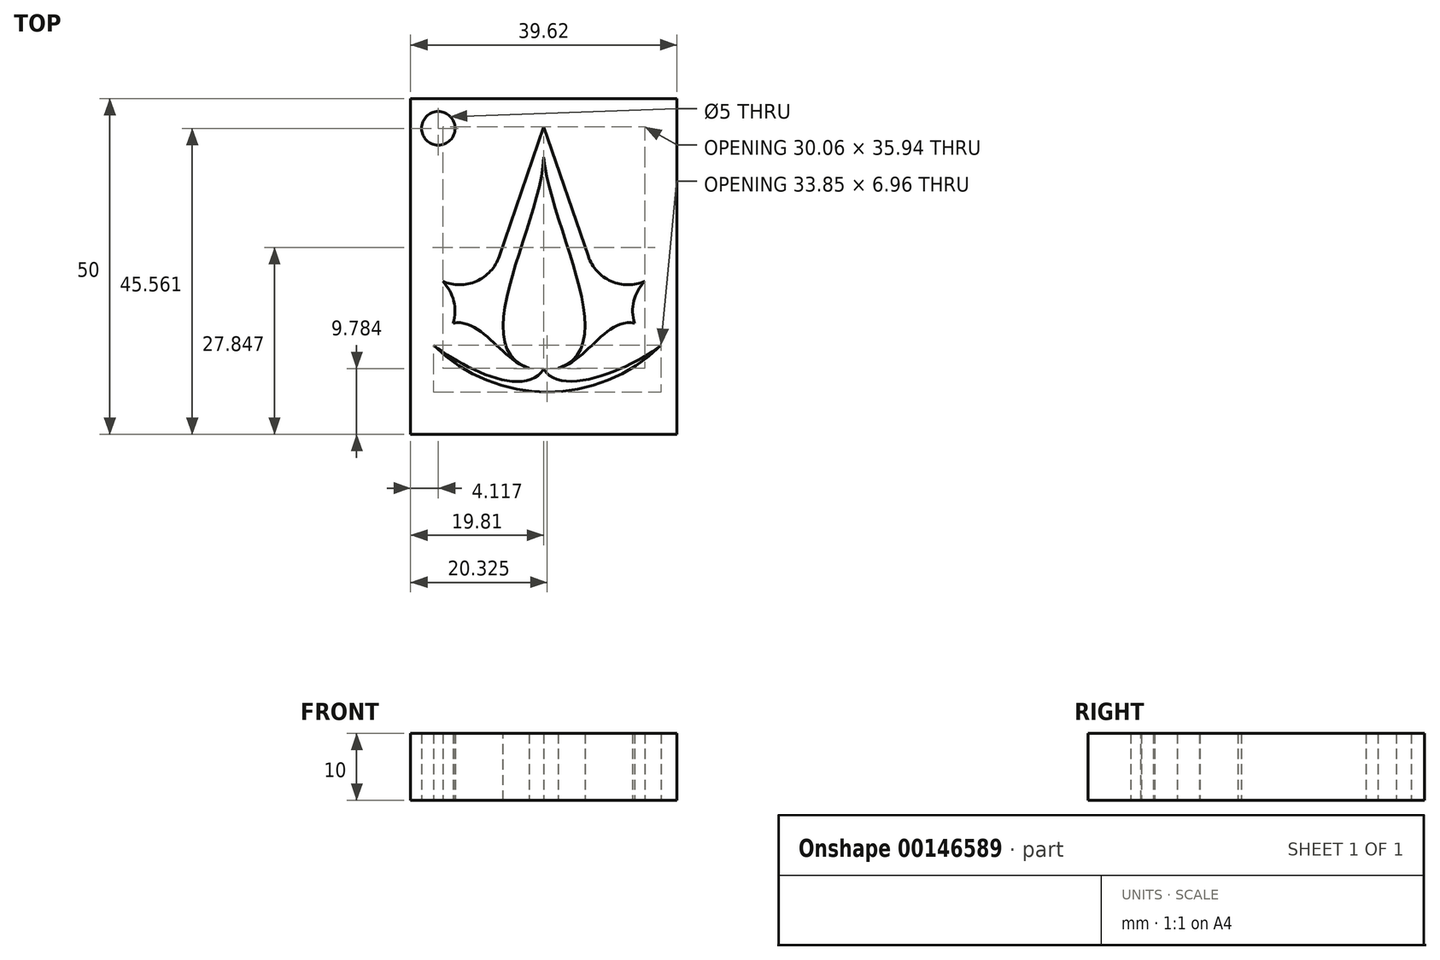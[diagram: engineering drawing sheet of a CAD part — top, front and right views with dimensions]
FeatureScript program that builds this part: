
annotation { "Feature Type Name" : "Feature", "Feature Type Description" : "" }
export const myFeature = defineFeature(function(context is Context, id is Id, definition is map)
    precondition{}
    {
        {
            var Q0;
            Q0=qCreatedBy(makeId("Top.planeOp"),FACE);
            var sketch = newSketch(context, id + "F0", { "sketchPlane" : qUnion([Q0])});
            skPoint(sketch, "E0", {"position": v(0, 23.04) * mm});
            skLineSegment(sketch, "E1", {"start": v(0, 23.04) * mm, "end": v(-6.63, 3.72) * mm});
            skLineSegment(sketch, "E2", {"start": v(0, 23.04) * mm, "end": v(6.63, 3.72) * mm});
            skPoint(sketch, "E3", {"position": v(-15.03, 0) * mm});
            skPoint(sketch, "E4", {"position": v(15.03, 0) * mm});
            skArc(sketch, "E5", {"start": v(-15.03, 0) * mm, "mid": v(-10.02, 0.03) * mm, "end": v(-6.63, 3.72) * mm});
            skArc(sketch, "E6", {"start": v(6.63, 3.72) * mm, "mid": v(10.02, 0.03) * mm, "end": v(15.03, 0) * mm});
            skPoint(sketch, "E7", {"position": v(-13.48, -6.24) * mm});
            skPoint(sketch, "E8", {"position": v(13.48, -6.24) * mm});
            skArc(sketch, "E9", {"start": v(-13.48, -6.24) * mm, "mid": v(-13.4, -2.9) * mm, "end": v(-15.03, 0) * mm});
            skArc(sketch, "E10", {"start": v(15.03, 0) * mm, "mid": v(13.4, -2.9) * mm, "end": v(13.48, -6.24) * mm});
            skPoint(sketch, "E11", {"position": v(0, -6.24) * mm});
            skLineSegment(sketch, "E12", {"start": v(0, -6.24) * mm, "end": v(-13.48, -6.24) * mm, "construction": true});
            skLineSegment(sketch, "E13", {"start": v(0, -6.24) * mm, "end": v(13.48, -6.24) * mm, "construction": true});
            skPoint(sketch, "E14", {"position": v(0, 3.72) * mm});
            skLineSegment(sketch, "E15", {"start": v(-6.63, 3.72) * mm, "end": v(0, 3.72) * mm, "construction": true});
            skLineSegment(sketch, "E16", {"start": v(0, 3.72) * mm, "end": v(6.63, 3.72) * mm, "construction": true});
            skPoint(sketch, "E17", {"position": v(-2.15, -12.9) * mm});
            skPoint(sketch, "E18", {"position": v(2.15, -12.9) * mm});
            skFitSpline(sketch, "E19", {"points": [v(-13.48, -6.24) * mm, v(-2.15, -12.9) * mm], "startDerivative": vector(12.7, 2.7) * mm, "endDerivative": vector(11.86, -2.84) * mm});
            skFitSpline(sketch, "E20", {"points": [v(13.48, -6.24) * mm, v(2.15, -12.9) * mm], "startDerivative": vector(-12.78, 2.7) * mm, "endDerivative": vector(-12.82, -2.84) * mm});
            skPoint(sketch, "E21", {"position": v(0, 18.52) * mm});
            skFitSpline(sketch, "E22", {"points": [v(-2.15, -12.9) * mm, v(0, 18.52) * mm], "startDerivative": vector(-29.03, 9.1) * mm, "endDerivative": vector(1.52, 31.2) * mm});
            skFitSpline(sketch, "E23", {"points": [v(2.15, -12.9) * mm, v(0, 18.52) * mm], "startDerivative": vector(28.93, 9.1) * mm, "endDerivative": vector(-2.78, 31.2) * mm});
            skPoint(sketch, "E24", {"position": v(0, -13.07) * mm});
            skPoint(sketch, "E25", {"position": v(-16.4, -9.52) * mm});
            skPoint(sketch, "E26", {"position": v(17.44, -9.52) * mm});
            skArc(sketch, "E27", {"start": v(-16.4, -9.52) * mm, "mid": v(0.52, -16.48) * mm, "end": v(17.44, -9.52) * mm});
            skFitSpline(sketch, "E28", {"points": [v(0, -13.07) * mm, v(-16.4, -9.52) * mm], "startDerivative": vector(-8.28, -13.09) * mm, "endDerivative": vector(-14.11, 10.88) * mm});
            skFitSpline(sketch, "E29", {"points": [v(0, -13.07) * mm, v(17.44, -9.52) * mm], "startDerivative": vector(7.56, -13.09) * mm, "endDerivative": vector(13.06, 10.25) * mm});
            skPoint(sketch, "E30.startSnap0", {"position": v(0.52, -16.48) * mm});
            skLineSegment(sketch, "E31.bottom", {"start": v(-19.8, -22.78) * mm, "end": v(19.8, -22.78) * mm});
            skLineSegment(sketch, "E31.top", {"start": v(-19.8, 27.22) * mm, "end": v(19.8, 27.22) * mm});
            skLineSegment(sketch, "E31.left", {"start": v(-19.8, -22.78) * mm, "end": v(-19.8, 27.22) * mm});
            skLineSegment(sketch, "E31.right", {"start": v(19.8, -22.78) * mm, "end": v(19.8, 27.22) * mm});
            skPoint(sketch, "E31.middle", {"position": v(0, 2.22) * mm});
            skCircle(sketch, "E32", {"center": v(-15.7, 22.78) * mm, "radius": 2.5 * mm});
            skSolve(sketch);
        }
        {
            var Q0;
            Q0 = qSketchRegion(id + "F0", true);
            extrude(context, id + "F1", {"entities" : qUnion([Q0]), "depth" : 10 * mm});
        }
    });
